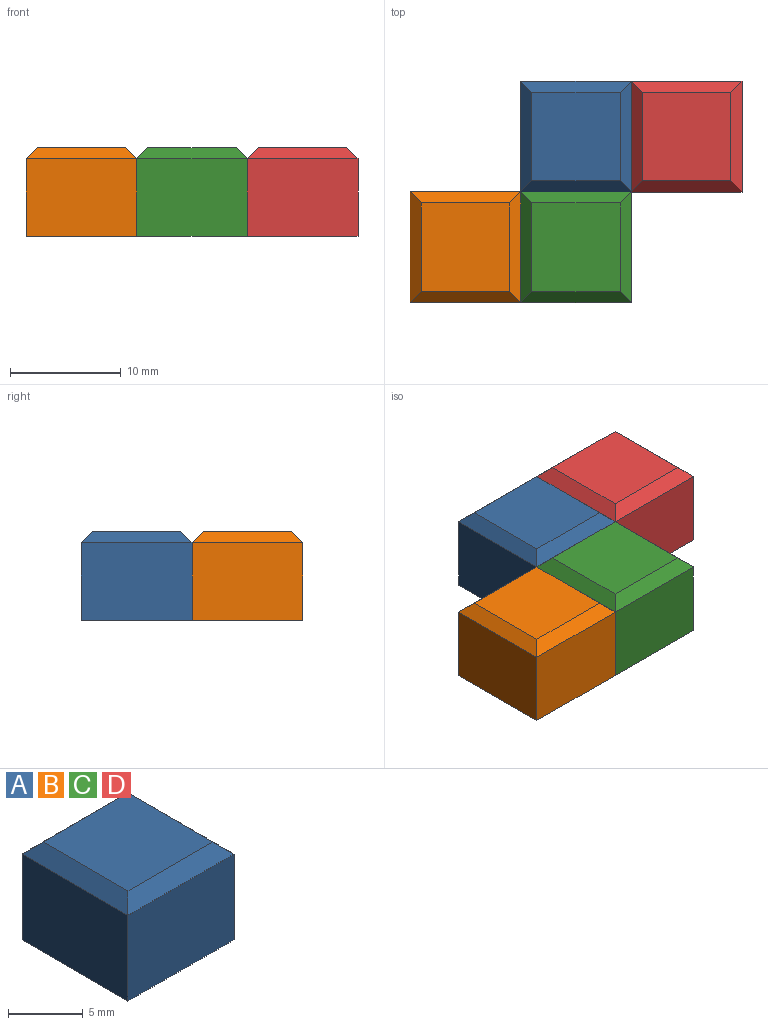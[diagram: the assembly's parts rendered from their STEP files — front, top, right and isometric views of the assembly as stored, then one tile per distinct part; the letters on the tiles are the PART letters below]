
ASSEMBLY  parts=4 mates=3
PART A: 10 faces, bbox 10x10x8 mm
  f0: plane 10x7mm, normal (0,1,0), area 70mm2, adj f1,f3,f5,f9
  f1: plane 10x7mm, normal (-1,0,0), area 70mm2, adj f0,f2,f5,f7
  f2: plane 10x7mm, normal (0,-1,0), area 70mm2, adj f1,f3,f5,f6
  f3: plane 10x7mm, normal (1,0,0), area 70mm2, adj f0,f2,f5,f8
  f4: plane 8x8mm, normal (0,0,1), area 64mm2, adj f6,f7,f8,f9
  f5: plane 10x10mm, normal (0,0,-1), area 100mm2, adj f0,f1,f2,f3
  f6: plane 10x1mm, normal (0,-0.71,0.71), area 12.7mm2, adj f2,f4,f7,f8
  f7: plane 10x1mm, normal (-0.71,0,0.71), area 12.7mm2, adj f1,f4,f6,f9
  f8: plane 10x1mm, normal (0.71,0,0.71), area 12.7mm2, adj f3,f4,f6,f9
  f9: plane 10x1mm, normal (0,0.71,0.71), area 12.7mm2, adj f0,f4,f7,f8
PART B: same geometry as A
PART C: same geometry as A
PART D: same geometry as A
PLACE A t=(30.93,6.73,4.22)mm
PLACE B t=(20.93,-3.27,4.22)mm
PLACE C t=(30.93,-3.27,4.22)mm
PLACE D t=(40.93,6.73,4.22)mm
MATE fastened A.f2 <-> C.f0  axis (0,-1,0) through (-6.49,6.73,7.72)mm
MATE fastened B.f3 <-> C.f1  axis (1,0,0) through (-11.49,1.73,7.72)mm
MATE fastened A.f3 <-> D.f1  axis (1,0,0) through (-1.49,11.73,7.72)mm
